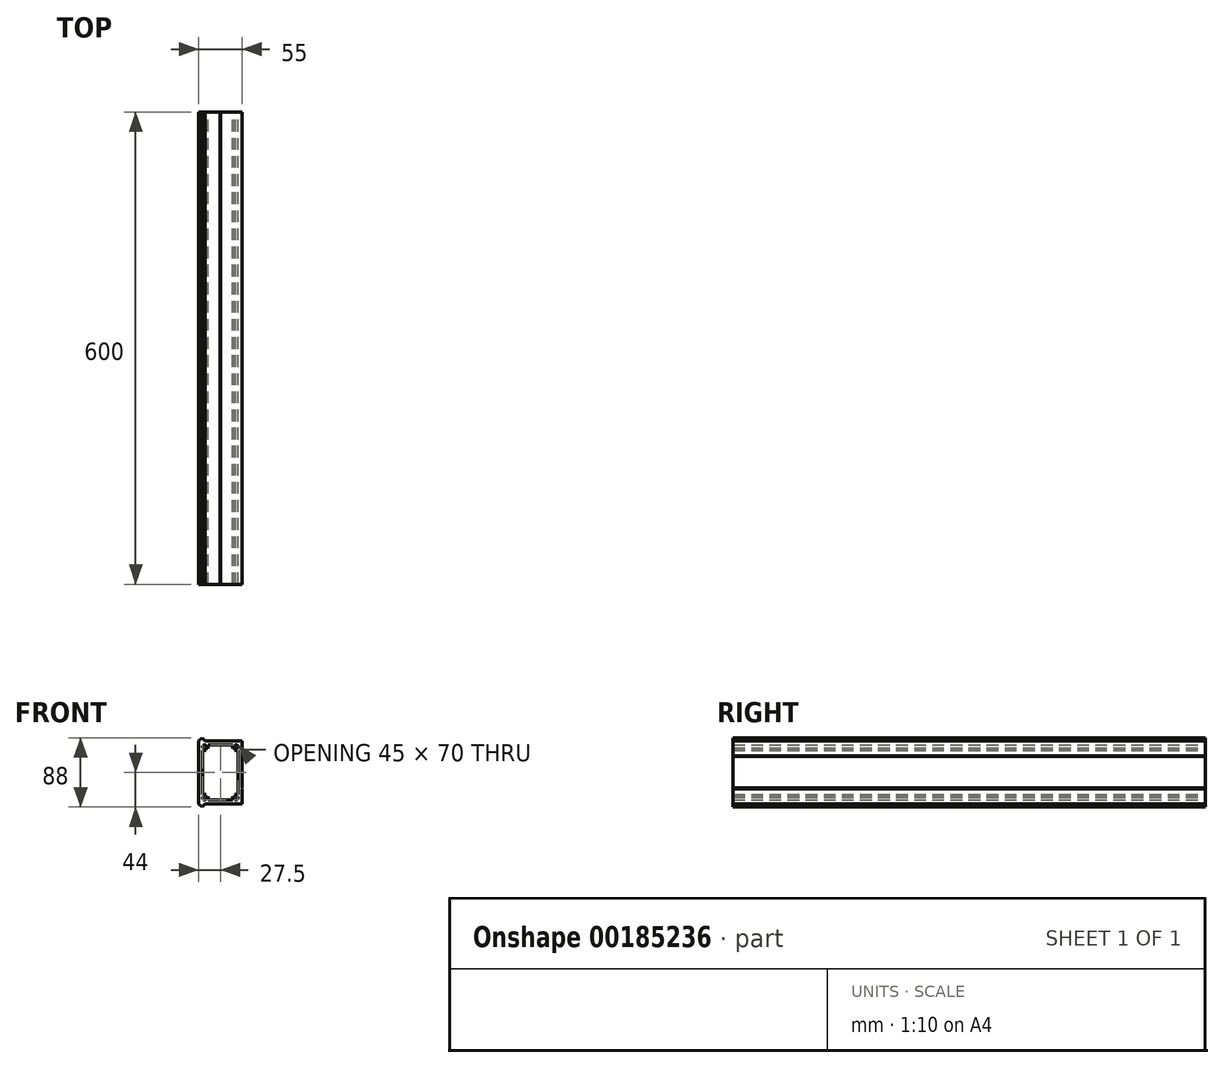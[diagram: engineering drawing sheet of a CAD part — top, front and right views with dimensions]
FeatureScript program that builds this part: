
annotation { "Feature Type Name" : "Feature", "Feature Type Description" : "" }
export const myFeature = defineFeature(function(context is Context, id is Id, definition is map)
    precondition{}
    {
        {
            var Q0;
            Q0=qCreatedBy(makeId("Front.planeOp"),FACE);
            var sketch = newSketch(context, id + "F0", { "sketchPlane" : qUnion([Q0])});
            skLineSegment(sketch, "E0", {"start": v(0, 0) * mm, "end": v(0, 80) * mm});
            skLineSegment(sketch, "E1", {"start": v(0, 80) * mm, "end": v(4, 84) * mm});
            skLineSegment(sketch, "E2", {"start": v(4, 84) * mm, "end": v(8, 80) * mm});
            skLineSegment(sketch, "E3", {"start": v(8, 80) * mm, "end": v(27, 80) * mm});
            skLineSegment(sketch, "E4", {"start": v(27, 80) * mm, "end": v(27.5, 79.5) * mm});
            skLineSegment(sketch, "E5", {"start": v(27.5, 79.5) * mm, "end": v(28, 80) * mm});
            skLineSegment(sketch, "E6", {"start": v(28, 80) * mm, "end": v(55, 80) * mm});
            skLineSegment(sketch, "E7", {"start": v(55, 80) * mm, "end": v(55, 61) * mm});
            skLineSegment(sketch, "E8", {"start": v(55, 61) * mm, "end": v(54.5, 60.5) * mm});
            skLineSegment(sketch, "E9", {"start": v(54.5, 60.5) * mm, "end": v(55, 60) * mm});
            skLineSegment(sketch, "E10", {"start": v(55, 60) * mm, "end": v(55, 20) * mm});
            skLineSegment(sketch, "E11", {"start": v(55, 20) * mm, "end": v(54.5, 19.5) * mm});
            skLineSegment(sketch, "E12", {"start": v(54.5, 19.5) * mm, "end": v(55, 19) * mm});
            skLineSegment(sketch, "E13", {"start": v(55, 19) * mm, "end": v(55, 0) * mm});
            skLineSegment(sketch, "E14", {"start": v(55, 0) * mm, "end": v(28, 0) * mm});
            skLineSegment(sketch, "E15", {"start": v(28, 0) * mm, "end": v(27.5, 0.5) * mm});
            skLineSegment(sketch, "E16", {"start": v(27.5, 0.5) * mm, "end": v(27, 0) * mm});
            skLineSegment(sketch, "E17", {"start": v(27, 0) * mm, "end": v(8, 0) * mm});
            skLineSegment(sketch, "E18", {"start": v(8, 0) * mm, "end": v(4, -4) * mm});
            skLineSegment(sketch, "E19", {"start": v(4, -4) * mm, "end": v(0, 0) * mm});
            skSolve(sketch);
        }
        {
            var Q0;
            Q0=makeQuery(id+"F0.imprint","IMPRINT",FACE,{"disambiguationData":[TD([[makeQuery(id+"F0.imprint","IMPRINT",EDGE,{"derivedFrom":sQuery(id+"F0.wireOp",EDGE,"E0")}),-1.0]])]});
            extrude(context, id + "F1", {"entities" : qUnion([Q0]), "depth" : 600 * mm});
        }
        {
            var Q0;
            Q0=qCreatedBy(makeId("Front.planeOp"),FACE);
            var sketch = newSketch(context, id + "F2", { "sketchPlane" : qUnion([Q0])});
            skLineSegment(sketch, "E20.bottom", {"start": v(7.5, 72.5) * mm, "end": v(47.5, 72.5) * mm, "construction": true});
            skLineSegment(sketch, "E20.top", {"start": v(7.5, 7.5) * mm, "end": v(47.5, 7.5) * mm, "construction": true});
            skLineSegment(sketch, "E20.left", {"start": v(7.5, 72.5) * mm, "end": v(7.5, 7.5) * mm, "construction": true});
            skLineSegment(sketch, "E20.right", {"start": v(47.5, 72.5) * mm, "end": v(47.5, 7.5) * mm, "construction": true});
            skLineSegment(sketch, "E21.bottom", {"start": v(5, 75) * mm, "end": v(50, 75) * mm, "construction": true});
            skLineSegment(sketch, "E21.top", {"start": v(5, 5) * mm, "end": v(50, 5) * mm, "construction": true});
            skLineSegment(sketch, "E21.left", {"start": v(5, 75) * mm, "end": v(5, 5) * mm, "construction": true});
            skLineSegment(sketch, "E21.right", {"start": v(50, 75) * mm, "end": v(50, 5) * mm, "construction": true});
            skLineSegment(sketch, "E22.bottom", {"start": v(9.4, 70.6) * mm, "end": v(45.6, 70.6) * mm, "construction": true});
            skLineSegment(sketch, "E22.top", {"start": v(9.4, 9.4) * mm, "end": v(45.6, 9.4) * mm, "construction": true});
            skLineSegment(sketch, "E22.left", {"start": v(9.4, 70.6) * mm, "end": v(9.4, 9.4) * mm, "construction": true});
            skLineSegment(sketch, "E22.right", {"start": v(45.6, 70.6) * mm, "end": v(45.6, 9.4) * mm, "construction": true});
            skLineSegment(sketch, "E23", {"start": v(9.4, 12) * mm, "end": v(5, 12) * mm});
            skLineSegment(sketch, "E24", {"start": v(5, 12) * mm, "end": v(5, 68) * mm});
            skLineSegment(sketch, "E25", {"start": v(5, 68) * mm, "end": v(9.4, 68) * mm});
            skLineSegment(sketch, "E26", {"start": v(9.4, 68) * mm, "end": v(12, 70.6) * mm, "construction": true});
            skLineSegment(sketch, "E27", {"start": v(12, 70.6) * mm, "end": v(12, 75) * mm});
            skLineSegment(sketch, "E28", {"start": v(12, 75) * mm, "end": v(43, 75) * mm});
            skLineSegment(sketch, "E29", {"start": v(43, 75) * mm, "end": v(43, 70.6) * mm});
            skLineSegment(sketch, "E30", {"start": v(43, 70.6) * mm, "end": v(45.6, 68) * mm, "construction": true});
            skLineSegment(sketch, "E31", {"start": v(45.6, 68) * mm, "end": v(50, 68) * mm});
            skLineSegment(sketch, "E32", {"start": v(50, 68) * mm, "end": v(50, 12) * mm});
            skLineSegment(sketch, "E33", {"start": v(50, 12) * mm, "end": v(45.6, 12) * mm});
            skLineSegment(sketch, "E34", {"start": v(45.6, 12) * mm, "end": v(43, 9.4) * mm, "construction": true});
            skLineSegment(sketch, "E35", {"start": v(43, 9.4) * mm, "end": v(43, 5) * mm});
            skLineSegment(sketch, "E36", {"start": v(43, 5) * mm, "end": v(12, 5) * mm});
            skLineSegment(sketch, "E37", {"start": v(12, 5) * mm, "end": v(12, 9.4) * mm});
            skLineSegment(sketch, "E38", {"start": v(12, 9.4) * mm, "end": v(9.4, 12) * mm, "construction": true});
            skArc(sketch, "E39", {"start": v(9.65, 71.23) * mm, "mid": v(5.73, 74.27) * mm, "end": v(8.77, 70.35) * mm});
            skLineSegment(sketch, "E40", {"start": v(8.77, 70.35) * mm, "end": v(9.4, 68) * mm});
            skLineSegment(sketch, "E41", {"start": v(9.65, 71.23) * mm, "end": v(12, 70.6) * mm});
            skLineSegment(sketch, "E42", {"start": v(7.5, 72.5) * mm, "end": v(9.4, 70.6) * mm, "construction": true});
            skLineSegment(sketch, "E43", {"start": v(9.65, 71.23) * mm, "end": v(8.77, 70.35) * mm, "construction": true});
            skPoint(sketch, "E44", {"position": v(9.21, 70.79) * mm});
            skArc(sketch, "E45", {"start": v(8.16, 9.91) * mm, "mid": v(5.73, 5.73) * mm, "end": v(9.91, 8.16) * mm});
            skLineSegment(sketch, "E46", {"start": v(9.4, 12) * mm, "end": v(8.16, 9.91) * mm});
            skLineSegment(sketch, "E47", {"start": v(12, 9.4) * mm, "end": v(9.91, 8.16) * mm});
            skArc(sketch, "E48", {"start": v(45.09, 8.16) * mm, "mid": v(49.27, 5.73) * mm, "end": v(46.84, 9.91) * mm});
            skLineSegment(sketch, "E49", {"start": v(43, 9.4) * mm, "end": v(45.09, 8.16) * mm});
            skLineSegment(sketch, "E50", {"start": v(45.6, 12) * mm, "end": v(46.84, 9.91) * mm});
            skArc(sketch, "E51", {"start": v(45.35, 71.23) * mm, "mid": v(49.27, 74.27) * mm, "end": v(46.23, 70.35) * mm});
            skLineSegment(sketch, "E52", {"start": v(45.35, 71.23) * mm, "end": v(46.23, 70.35) * mm, "construction": true});
            skLineSegment(sketch, "E53", {"start": v(47.5, 72.5) * mm, "end": v(44.3, 69.3) * mm, "construction": true});
            skPoint(sketch, "E54", {"position": v(45.79, 70.79) * mm});
            skLineSegment(sketch, "E55", {"start": v(45.35, 71.23) * mm, "end": v(43, 70.6) * mm});
            skLineSegment(sketch, "E56", {"start": v(46.23, 70.35) * mm, "end": v(45.6, 68) * mm});
            skSolve(sketch);
        }
        {
            var Q0;
            Q0 = qSketchRegion(id + "F2", true);
            extrude(context, id + "F3", {"entities" : qUnion([Q0]), "operationType" : NewBodyOperationType.REMOVE, "endBound" : BoundingType.UP_TO_NEXT, "depth" : 600 * mm});
        }
    });
